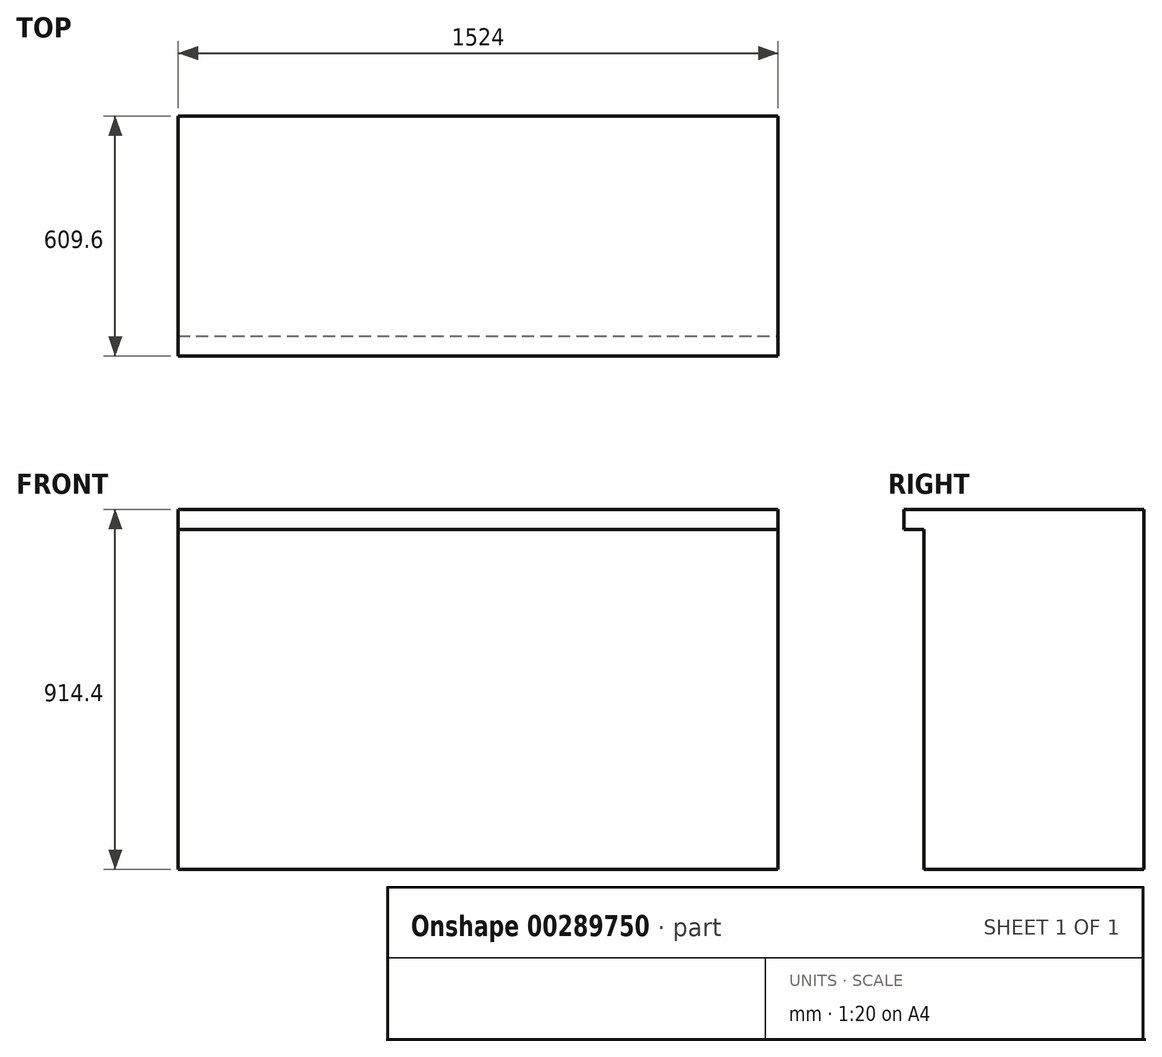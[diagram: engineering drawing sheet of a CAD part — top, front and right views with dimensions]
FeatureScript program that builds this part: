
annotation { "Feature Type Name" : "Feature", "Feature Type Description" : "" }
export const myFeature = defineFeature(function(context is Context, id is Id, definition is map)
    precondition{}
    {
        {
            var Q0;
            Q0=qCreatedBy(makeId("Top.planeOp"),FACE);
            var sketch = newSketch(context, id + "F0", { "sketchPlane" : qUnion([Q0])});
            skLineSegment(sketch, "E0.bottom", {"start": v(762, -304.8) * mm, "end": v(-762, -304.8) * mm});
            skLineSegment(sketch, "E0.top", {"start": v(762, 304.8) * mm, "end": v(-762, 304.8) * mm});
            skLineSegment(sketch, "E0.left", {"start": v(762, -304.8) * mm, "end": v(762, 304.8) * mm});
            skLineSegment(sketch, "E0.right", {"start": v(-762, -304.8) * mm, "end": v(-762, 304.8) * mm});
            skPoint(sketch, "E0.middle", {"position": v(0, 0) * mm});
            skSolve(sketch);
        }
        {
            var Q0;
            Q0=makeQuery(id+"F0.imprint","IMPRINT",FACE,{"disambiguationData":[TD([[makeQuery(id+"F0.imprint","IMPRINT",EDGE,{"derivedFrom":sQuery(id+"F0.wireOp",EDGE,"E0.bottom")}),-1.0]])]});
            extrude(context, id + "F1", {"entities" : qUnion([Q0]), "depth" : 914.4 * mm, "offsetDistance" : 30.48 * mm});
        }
        {
            var Q0;
            Q0=makeQuery(id+"F1.opExtrude","SWEPT_FACE",FACE,{"disambiguationData":[OSD([sQuery(id+"F0.wireOp",EDGE,"E0.left")])]});
            var sketch = newSketch(context, id + "F2", { "sketchPlane" : qUnion([Q0])});
            skLineSegment(sketch, "E1.bottom", {"start": v(-304.8, 863.6) * mm, "end": v(-254, 863.6) * mm});
            skLineSegment(sketch, "E1.top", {"start": v(-304.8, 0) * mm, "end": v(-254, 0) * mm});
            skLineSegment(sketch, "E1.left", {"start": v(-304.8, 863.6) * mm, "end": v(-304.8, 0) * mm});
            skLineSegment(sketch, "E1.right", {"start": v(-254, 863.6) * mm, "end": v(-254, 0) * mm});
            skSolve(sketch);
        }
        {
            var Q0;
            Q0=makeQuery(id+"F2.imprint","IMPRINT",FACE,{"disambiguationData":[TD([[makeQuery(id+"F2.imprint","IMPRINT",EDGE,{"derivedFrom":sQuery(id+"F2.wireOp",EDGE,"E1.bottom")}),-1.0]])]});
            extrude(context, id + "F3", {"entities" : qUnion([Q0]), "operationType" : NewBodyOperationType.REMOVE, "oppositeDirection" : true, "depth" : 3048 * mm, "offsetDistance" : 30.48 * mm});
        }
    });
